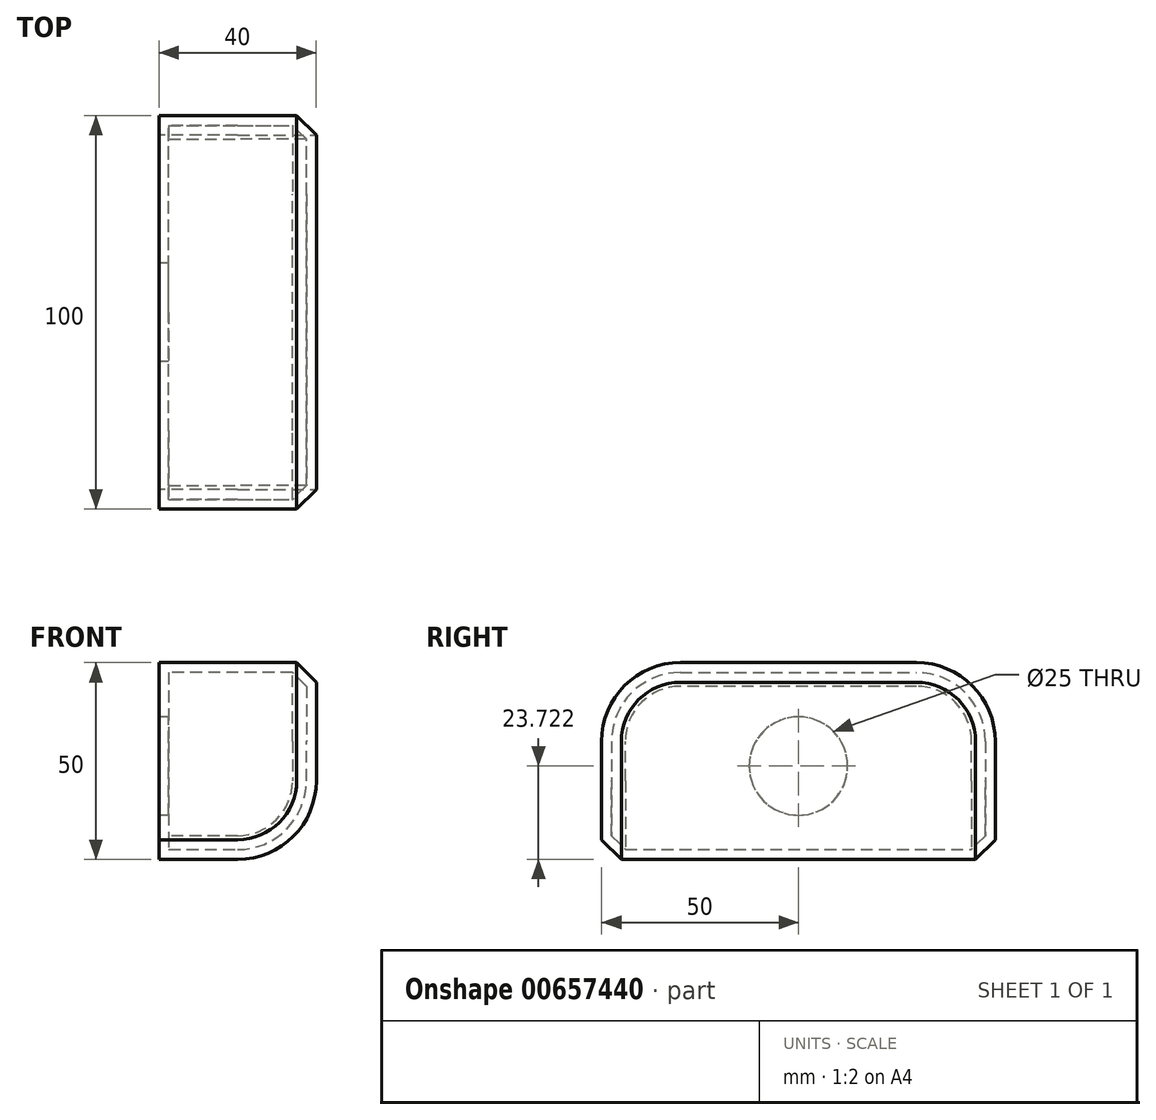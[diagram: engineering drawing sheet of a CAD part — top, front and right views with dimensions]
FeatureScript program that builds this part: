
annotation { "Feature Type Name" : "Feature", "Feature Type Description" : "" }
export const myFeature = defineFeature(function(context is Context, id is Id, definition is map)
    precondition{}
    {
        {
            var Q0;
            Q0=qCreatedBy(makeId("Front.planeOp"),FACE);
            var sketch = newSketch(context, id + "F0", { "sketchPlane" : qUnion([Q0])});
            skLineSegment(sketch, "E0.bottom", {"start": v(29.33, 38.94) * mm, "end": v(-10.67, 38.94) * mm});
            skLineSegment(sketch, "E0.top", {"start": v(29.33, -11.06) * mm, "end": v(-10.67, -11.06) * mm});
            skLineSegment(sketch, "E0.left", {"start": v(29.33, 38.94) * mm, "end": v(29.33, -11.06) * mm});
            skLineSegment(sketch, "E0.right", {"start": v(-10.67, 38.94) * mm, "end": v(-10.67, -11.06) * mm});
            skSolve(sketch);
        }
        {
            var Q0;
            Q0=makeQuery(id+"F0.imprint","IMPRINT",FACE,{"disambiguationData":[TD([[makeQuery(id+"F0.imprint","IMPRINT",EDGE,{"derivedFrom":sQuery(id+"F0.wireOp",EDGE,"E0.bottom")}),1.0]])]});
            extrude(context, id + "F1", {"entities" : qUnion([Q0]), "depth" : 50 * mm, "offsetDistance" : 25 * mm});
        }
        {
            var Q0;
            Q0=makeQuery(id+"F1.opExtrude","CAP_EDGE",EDGE,{"disambiguationData":[OSD([sQuery(id+"F0.wireOp",EDGE,"E0.bottom")])],"isStart":false});
            var Q1;
            Q1=makeQuery(id+"F1.opExtrude","SWEPT_EDGE",EDGE,{"disambiguationData":[OSD([sQuery(id+"F0.wireOp",EDGE,"E0.top"),sQuery(id+"F0.wireOp",EDGE,"E0.left")])]});
            fillet(context, id + "F2", {"entities" : qUnion([Q0, Q1]), "radius" : 20 * mm, "tangentPropagation" : true, "allowEdgeOverflow" : false});
        }
        {
            var Q0;
            Q0=makeQuery(id+"F1.opExtrude","SWEPT_EDGE",EDGE,{"disambiguationData":[OSD([sQuery(id+"F0.wireOp",EDGE,"E0.bottom"),sQuery(id+"F0.wireOp",EDGE,"E0.left")])]});
            chamfer(context, id + "F3", {"entities" : qUnion([Q0]), "width" : 5 * mm, "tangentPropagation" : true});
        }
        {
            var Q0;
            Q0=makeQuery(id+"F1.opExtrude","CAP_FACE",FACE,{"disambiguationData":[OSD([sQuery(id+"F0.wireOp",EDGE,"E0.bottom"),sQuery(id+"F0.wireOp",EDGE,"E0.top"),sQuery(id+"F0.wireOp",EDGE,"E0.left"),sQuery(id+"F0.wireOp",EDGE,"E0.right")])],"isStart":true});
            shell(context, id + "F4", {"entities" : qUnion([Q0]), "thickness" : 2.5 * mm});
        }
        {
            var Q0;
            Q0=makeQuery(id+"F1.opExtrude","SWEPT_BODY",BODY,{"disambiguationData":[OSD([sQuery(id+"F0.wireOp",EDGE,"E0.bottom"),sQuery(id+"F0.wireOp",EDGE,"E0.top"),sQuery(id+"F0.wireOp",EDGE,"E0.left"),sQuery(id+"F0.wireOp",EDGE,"E0.right")])]});
            var Q1;
            Q1=qCreatedBy(makeId("Front.planeOp"),FACE);
            mirror(context, id + "F5", {"operationType" : NewBodyOperationType.ADD, "entities" : qUnion([Q0]), "mirrorPlane" : qUnion([Q1])});
        }
        {
            var Q0;
            {var subQ0=makeQuery(id+"F1.opExtrude","SWEPT_FACE",FACE,{"disambiguationData":[OSD([sQuery(id+"F0.wireOp",EDGE,"E0.right")])]});Q0=makeQuery(id+"F5.boolean.opBoolean","MERGE",FACE,{"derivedFrom":[subQ0,makeQuery(id+"F5.opPattern","COPY",FACE,{"derivedFrom":subQ0,"instanceName":"1"})]});}
            var sketch = newSketch(context, id + "F6", { "sketchPlane" : qUnion([Q0])});
            skCircle(sketch, "E1", {"center": v(0, 12.66) * mm, "radius": 12.5 * mm});
            skSolve(sketch);
        }
        {
            var Q0;
            Q0=makeQuery(id+"F6.imprint","IMPRINT",FACE,{"disambiguationData":[TD([[makeQuery(id+"F6.imprint","IMPRINT",EDGE,{"derivedFrom":sQuery(id+"F6.wireOp",EDGE,"E1")}),1.0]])]});
            extrude(context, id + "F7", {"entities" : qUnion([Q0]), "operationType" : NewBodyOperationType.REMOVE, "endBound" : BoundingType.UP_TO_NEXT, "oppositeDirection" : true, "depth" : 25 * mm, "offsetDistance" : 25 * mm});
        }
    });
